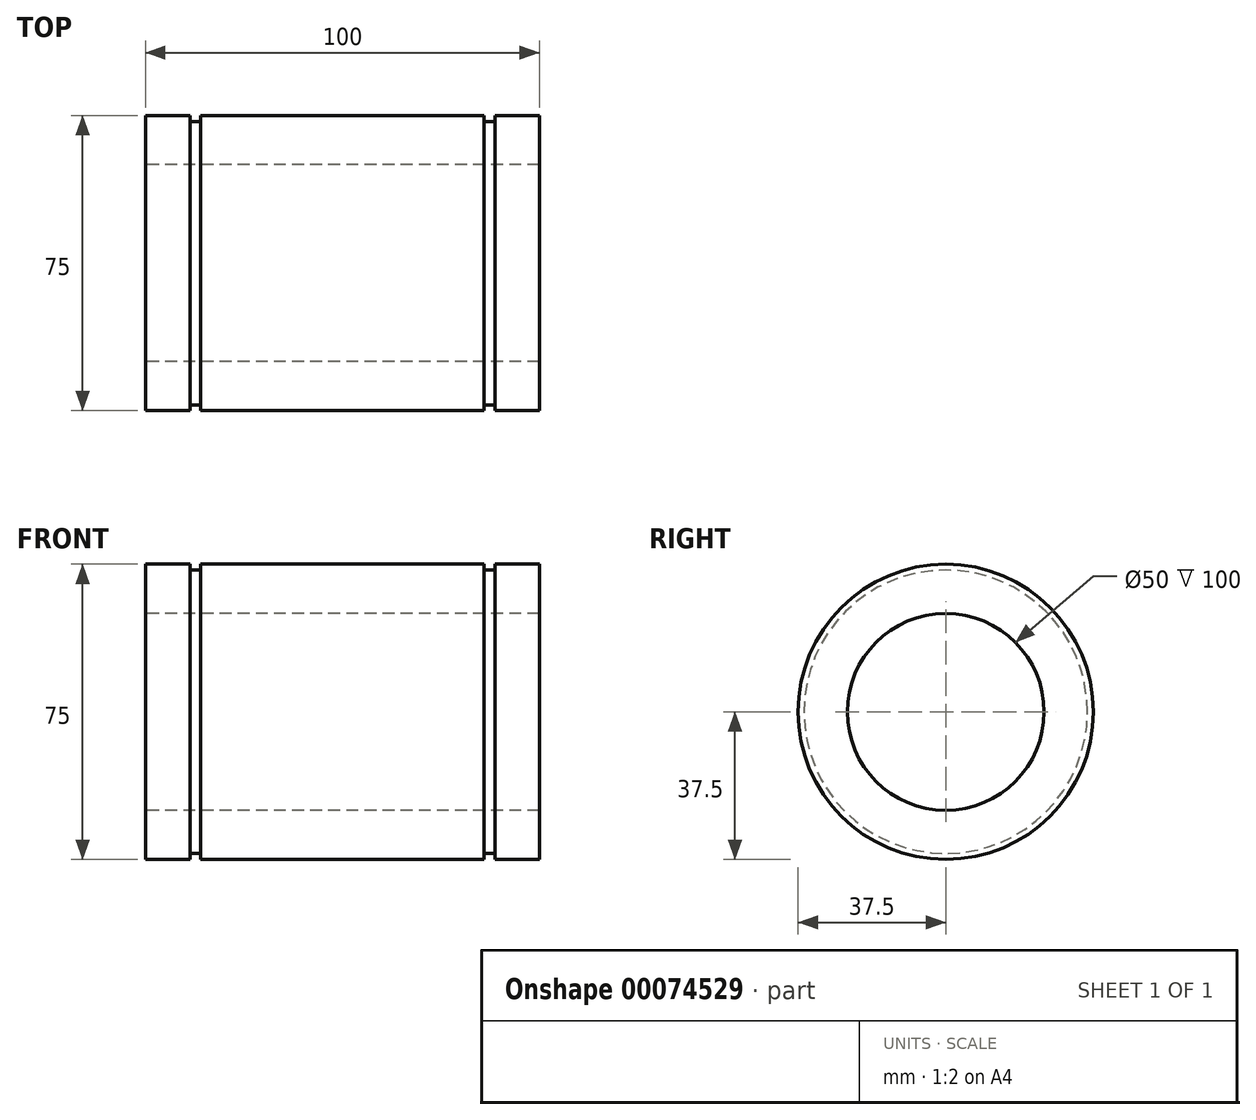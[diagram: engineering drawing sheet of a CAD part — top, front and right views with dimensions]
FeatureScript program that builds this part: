
annotation { "Feature Type Name" : "Feature", "Feature Type Description" : "" }
export const myFeature = defineFeature(function(context is Context, id is Id, definition is map)
    precondition{}
    {
        {
            var Q0;
            Q0=qCreatedBy(makeId("Front.planeOp"),FACE);
            var sketch = newSketch(context, id + "F0", { "sketchPlane" : qUnion([Q0])});
            skLineSegment(sketch, "E0", {"start": v(0, -2.02) * mm, "end": v(0, 37.5) * mm});
            skLineSegment(sketch, "E1", {"start": v(0, 37.5) * mm, "end": v(11.3, 37.5) * mm});
            skLineSegment(sketch, "E2", {"start": v(11.3, 37.5) * mm, "end": v(11.3, 36) * mm});
            skLineSegment(sketch, "E3", {"start": v(11.3, 36) * mm, "end": v(14, 36) * mm});
            skLineSegment(sketch, "E4", {"start": v(14, 36) * mm, "end": v(14, 37.5) * mm});
            skLineSegment(sketch, "E5", {"start": v(14, 37.5) * mm, "end": v(86, 37.5) * mm});
            skLineSegment(sketch, "E6", {"start": v(86, 37.5) * mm, "end": v(86, 36) * mm});
            skLineSegment(sketch, "E7", {"start": v(86, 36) * mm, "end": v(88.7, 36) * mm});
            skLineSegment(sketch, "E8", {"start": v(88.7, 36) * mm, "end": v(88.7, 37.5) * mm});
            skLineSegment(sketch, "E9", {"start": v(88.7, 37.5) * mm, "end": v(100, 37.5) * mm});
            skLineSegment(sketch, "E10", {"start": v(100, 37.5) * mm, "end": v(100, 0) * mm});
            skLineSegment(sketch, "E11", {"start": v(0, 25) * mm, "end": v(100, 25) * mm});
            skLineSegment(sketch, "E12", {"start": v(0, 0) * mm, "end": v(100, 0) * mm});
            skSolve(sketch);
        }
        {
            var Q0;
            {var subQ0=sQuery(id+"F0.wireOp",EDGE,"E1");Q0=makeQuery(id+"F0.imprint","IMPRINT",FACE,{"disambiguationData":[TD([[makeQuery(id+"F0.imprint","IMPRINT",EDGE,{"derivedFrom":subQ0}),-1.0]])]});}
            var Q1;
            Q1=sQuery(id+"F0.wireOp",EDGE,"E12");
            revolve(context, id + "F1", {"entities" : qUnion([Q0]), "axis" : qUnion([Q1]), "revolveType" : RevolveType.FULL});
        }
    });
